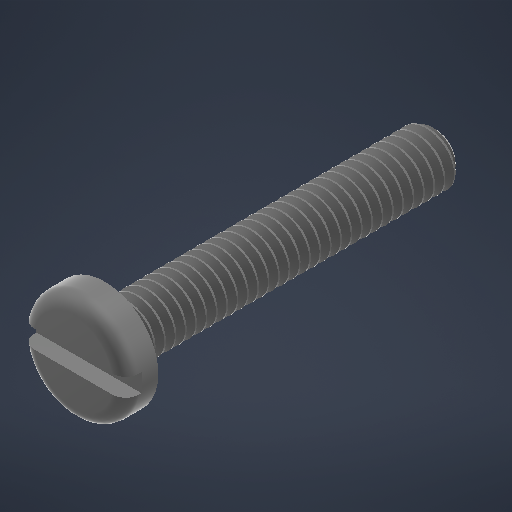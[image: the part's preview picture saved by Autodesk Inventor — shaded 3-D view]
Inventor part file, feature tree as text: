
AUTODESK INVENTOR PART (.ipt)
format: ipt  version: 2025.2 (Build 292293000, 293)  size: 561,664 bytes
history: native  units: in
note: dims shown in document units (in); Inventor stores cm internally (conversion verified against a paired STEP export)
features: other x1, extrude x1
ambient origin geometry x8: Origin, YZ Plane, XZ Plane, XY Plane, X Axis, Y Axis, Z Axis, Center Point
bodies: Solid1 (feature_tree)
feature tree (2):
  other  "Plane1"
  extrude  "Extrude15"  [1 undecoded]
note: 1 required parameter value undecoded (feature->parameter linkage not recoverable at this tier; creation-order binding heuristic only, values carry confidence <= 0.55)
